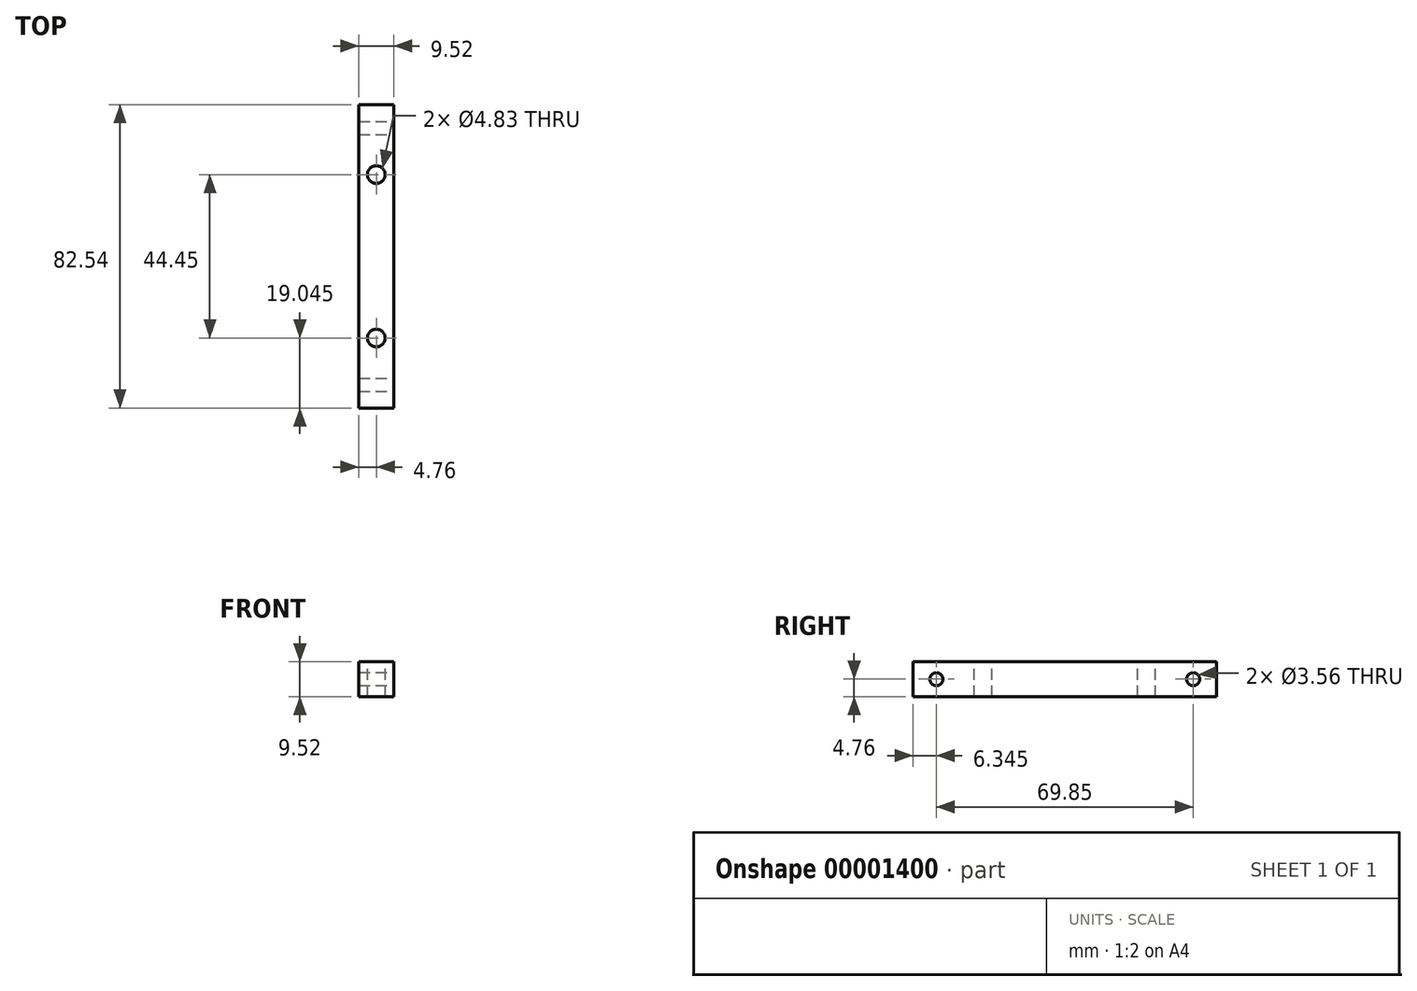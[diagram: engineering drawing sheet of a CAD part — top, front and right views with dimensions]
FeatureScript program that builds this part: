
annotation { "Feature Type Name" : "Feature", "Feature Type Description" : "" }
export const myFeature = defineFeature(function(context is Context, id is Id, definition is map)
    precondition{}
    {
        {
            var Q0;
            Q0=qCreatedBy(makeId("Front.planeOp"),FACE);
            var sketch = newSketch(context, id + "F0", { "sketchPlane" : qUnion([Q0])});
            skLineSegment(sketch, "E0.rect.bottom", {"start": v(4.76, 4.76) * mm, "end": v(-4.76, 4.76) * mm});
            skLineSegment(sketch, "E0.rect.top", {"start": v(4.76, -4.76) * mm, "end": v(-4.76, -4.76) * mm});
            skLineSegment(sketch, "E0.rect.left", {"start": v(4.76, 4.76) * mm, "end": v(4.76, -4.76) * mm});
            skLineSegment(sketch, "E0.rect.right", {"start": v(-4.76, 4.76) * mm, "end": v(-4.76, -4.76) * mm});
            skPoint(sketch, "E0.rect.middle", {"position": v(0, 0) * mm});
            skSolve(sketch);
        }
        {
            var Q0;
            Q0 = qSketchRegion(id + "F0", true);
            extrude(context, id + "F1", {"entities" : qUnion([Q0]), "endBound" : BoundingType.SYMMETRIC, "depth" : 82.55 * mm});
        }
        {
            var Q0;
            Q0=makeQuery(id+"F1.opExtrude","SWEPT_FACE",FACE,{"disambiguationData":[OSD([sQuery(id+"F0.wireOp",EDGE,"E0.rect.left")])]});
            var sketch = newSketch(context, id + "F2", { "sketchPlane" : qUnion([Q0])});
            skCircle(sketch, "E1", {"center": v(-34.93, 0) * mm, "radius": 1.78 * mm});
            skCircle(sketch, "E2", {"center": v(34.92, 0) * mm, "radius": 1.78 * mm});
            skSolve(sketch);
        }
        {
            var Q0;
            Q0 = qSketchRegion(id + "F2", true);
            extrude(context, id + "F3", {"entities" : qUnion([Q0]), "operationType" : NewBodyOperationType.REMOVE, "endBound" : BoundingType.THROUGH_ALL, "oppositeDirection" : true, "depth" : 25.4 * mm});
        }
        {
            var Q0;
            Q0=makeQuery(id+"F1.opExtrude","SWEPT_FACE",FACE,{"disambiguationData":[OSD([sQuery(id+"F0.wireOp",EDGE,"E0.rect.bottom")])]});
            var sketch = newSketch(context, id + "F4", { "sketchPlane" : qUnion([Q0])});
            skCircle(sketch, "E3", {"center": v(0, -22.23) * mm, "radius": 2.41 * mm});
            skCircle(sketch, "E4", {"center": v(0, 22.22) * mm, "radius": 2.41 * mm});
            skSolve(sketch);
        }
        {
            var Q0;
            Q0 = qSketchRegion(id + "F4", true);
            extrude(context, id + "F5", {"entities" : qUnion([Q0]), "operationType" : NewBodyOperationType.REMOVE, "endBound" : BoundingType.THROUGH_ALL, "oppositeDirection" : true, "depth" : 25.4 * mm});
        }
    });
